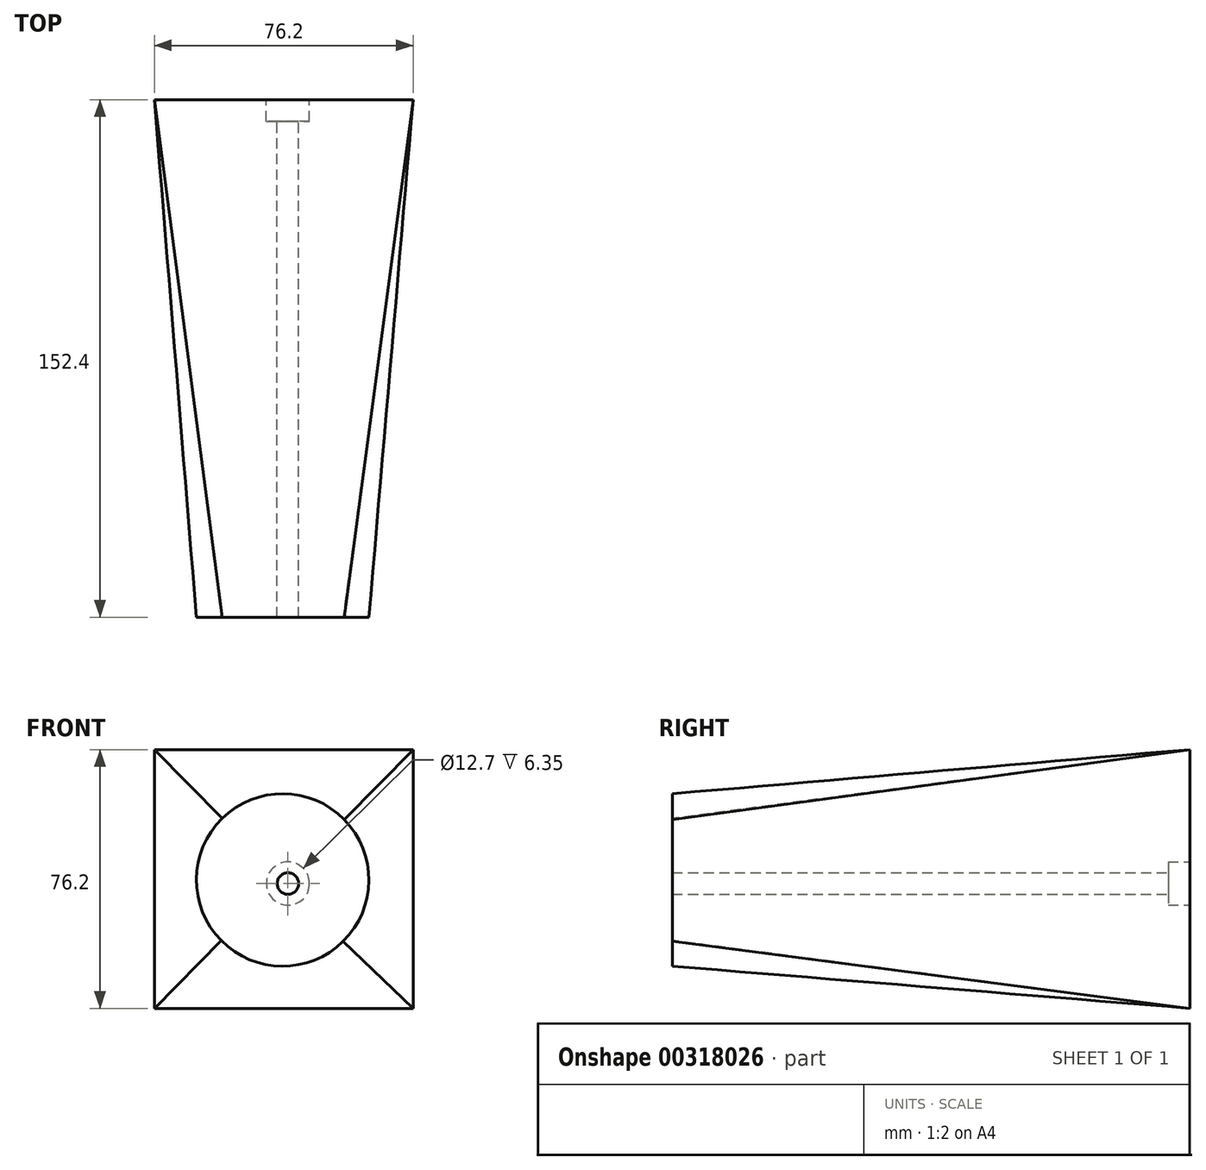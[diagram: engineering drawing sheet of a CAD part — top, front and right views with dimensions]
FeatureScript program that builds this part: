
annotation { "Feature Type Name" : "Feature", "Feature Type Description" : "" }
export const myFeature = defineFeature(function(context is Context, id is Id, definition is map)
    precondition{}
    {
        {
            var Q0;
            Q0=qCreatedBy(makeId("Front.planeOp"),FACE);
            var sketch = newSketch(context, id + "F0", { "sketchPlane" : qUnion([Q0])});
            skLineSegment(sketch, "E0.bottom", {"start": v(-42.73, 43.11) * mm, "end": v(33.47, 43.11) * mm});
            skLineSegment(sketch, "E0.top", {"start": v(-42.73, -33.09) * mm, "end": v(33.47, -33.09) * mm});
            skLineSegment(sketch, "E0.left", {"start": v(-42.73, 43.11) * mm, "end": v(-42.73, -33.09) * mm});
            skLineSegment(sketch, "E0.right", {"start": v(33.47, 43.11) * mm, "end": v(33.47, -33.09) * mm});
            skSolve(sketch);
        }
        {
            var Q0;
            Q0=qCreatedBy(makeId("Front.planeOp"),FACE);
            cPlane(context, id + "F1", {"entities" : qUnion([Q0]), "cplaneType" : CPlaneType.OFFSET, "offset" : 152.4 * mm, "width" : 152.4 * mm, "height" : 152.4 * mm});
        }
        {
            var Q0;
            Q0=qCreatedBy(id+"F1.planeOp",FACE);
            var sketch = newSketch(context, id + "F2", { "sketchPlane" : qUnion([Q0])});
            skCircle(sketch, "E1", {"center": v(-4.94, 4.73) * mm, "radius": 25.4 * mm});
            skSolve(sketch);
        }
        {
            var Q0;
            Q0=makeQuery(id+"F0.imprint","IMPRINT",FACE,{"disambiguationData":[TD([[makeQuery(id+"F0.imprint","IMPRINT",EDGE,{"derivedFrom":sQuery(id+"F0.wireOp",EDGE,"E0.bottom")}),-1.0]])]});
            var Q1;
            Q1=makeQuery(id+"F2.imprint","IMPRINT",FACE,{"disambiguationData":[TD([[makeQuery(id+"F2.imprint","IMPRINT",EDGE,{"derivedFrom":sQuery(id+"F2.wireOp",EDGE,"E1")}),1.0]])]});
            loft(context, id + "F3", {"sheetProfilesArray" : [{ "sheetProfileEntities" : qUnion([Q0]) }, { "sheetProfileEntities" : qUnion([Q1]) }]});
        }
        {
            var Q0;
            Q0=makeQuery(id+"F3.opLoft","CAP_FACE",FACE,{"disambiguationData":[OSD([makeQuery(id+"F0.imprint","IMPRINT",FACE,{"disambiguationData":[TD([[makeQuery(id+"F0.imprint","IMPRINT",EDGE,{"derivedFrom":sQuery(id+"F0.wireOp",EDGE,"E0.bottom")}),-1.0]])]})])],"isStart":true});
            var sketch = newSketch(context, id + "F4", { "sketchPlane" : qUnion([Q0])});
            skCircle(sketch, "E2", {"center": v(3.38, 3.66) * mm, "radius": 12.7 * mm});
            skSolve(sketch);
        }
        {
            var Q0;
            Q0=sQuery(id+"F4.wireOp",VERTEX,"E2.center");
            var Q1;
            Q1=makeQuery(id+"F3.opLoft","SWEPT_BODY",BODY,{"disambiguationData":[OSD([makeQuery(id+"F0.imprint","IMPRINT",FACE,{"disambiguationData":[TD([[makeQuery(id+"F0.imprint","IMPRINT",EDGE,{"derivedFrom":sQuery(id+"F0.wireOp",EDGE,"E0.bottom")}),-1.0]])]}),makeQuery(id+"F2.imprint","IMPRINT",FACE,{"disambiguationData":[TD([[makeQuery(id+"F2.imprint","IMPRINT",EDGE,{"derivedFrom":sQuery(id+"F2.wireOp",EDGE,"E1")}),1.0]])]})])]});
            hole(context, id + "F5", {"style" : HoleStyle.C_BORE, "endStyle" : HoleEndStyle.THROUGH, "holeDiameter" : 6.35 * mm, "cBoreDiameter" : 12.7 * mm, "cBoreDepth" : 6.35 * mm, "tappedDepth" : 12.7 * mm, "tapClearance" : 3, "locations" : qUnion([Q0]), "scope" : qUnion([Q1])});
        }
    });
